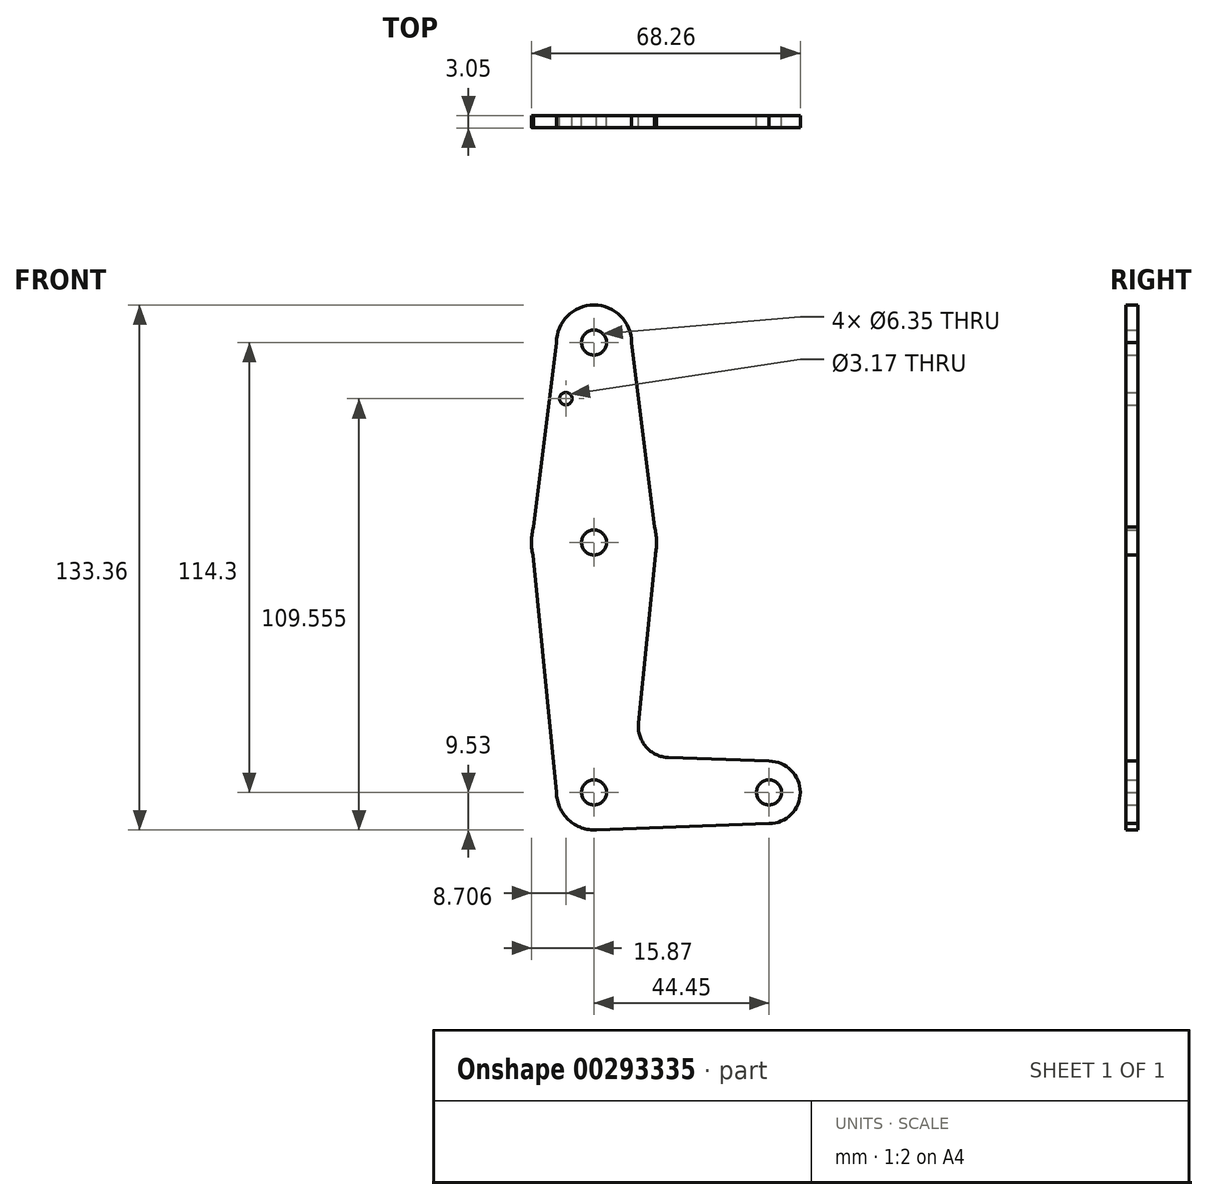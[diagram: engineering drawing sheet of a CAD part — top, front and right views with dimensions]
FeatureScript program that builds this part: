
annotation { "Feature Type Name" : "Feature", "Feature Type Description" : "" }
export const myFeature = defineFeature(function(context is Context, id is Id, definition is map)
    precondition{}
    {
        {
            var Q0;
            Q0=qCreatedBy(makeId("Front.planeOp"),FACE);
            var sketch = newSketch(context, id + "F0", { "sketchPlane" : qUnion([Q0])});
            skCircle(sketch, "E0", {"center": v(0, 0) * mm, "radius": 9.53 * mm});
            skLineSegment(sketch, "E1", {"start": v(0, 0) * mm, "end": v(0, 63.5) * mm, "construction": true});
            skCircle(sketch, "E2", {"center": v(0, 63.5) * mm, "radius": 15.88 * mm});
            skLineSegment(sketch, "E3", {"start": v(0, 63.5) * mm, "end": v(0, 114.3) * mm, "construction": true});
            skCircle(sketch, "E4", {"center": v(0, 114.3) * mm, "radius": 9.53 * mm});
            skLineSegment(sketch, "E5", {"start": v(0, 0) * mm, "end": v(44.45, 0) * mm, "construction": true});
            skCircle(sketch, "E6", {"center": v(44.45, 0) * mm, "radius": 7.94 * mm});
            skLineSegment(sketch, "E7", {"start": v(0, -9.53) * mm, "end": v(44.45, -7.94) * mm});
            skCircle(sketch, "E8", {"center": v(0, 114.3) * mm, "radius": 3.18 * mm});
            skCircle(sketch, "E9", {"center": v(0, 63.5) * mm, "radius": 3.17 * mm});
            skCircle(sketch, "E10", {"center": v(0, 0) * mm, "radius": 3.17 * mm});
            skCircle(sketch, "E11", {"center": v(44.45, 0) * mm, "radius": 3.17 * mm});
            skCircle(sketch, "E12", {"center": v(-7.16, 100.03) * mm, "radius": 1.59 * mm});
            skLineSegment(sketch, "E13", {"start": v(-9.52, 114.3) * mm, "end": v(-15.88, 63.5) * mm});
            skLineSegment(sketch, "E14", {"start": v(9.52, 114.3) * mm, "end": v(15.88, 63.5) * mm});
            skLineSegment(sketch, "E15", {"start": v(44.45, 7.94) * mm, "end": v(18.91, 8.85) * mm});
            skLineSegment(sketch, "E16", {"start": v(15.88, 63.5) * mm, "end": v(11.28, 17.59) * mm});
            skPoint(sketch, "E17.newPointA", {"position": v(9.52, 0) * mm});
            skPoint(sketch, "E17.newPointB", {"position": v(0, 9.53) * mm});
            skArc(sketch, "E17.filletArc", {"start": v(11.28, 17.59) * mm, "mid": v(13.2, 11.57) * mm, "end": v(18.91, 8.85) * mm});
            skLineSegment(sketch, "E18", {"start": v(-15.88, 63.5) * mm, "end": v(-9.52, 0) * mm});
            skSolve(sketch);
        }
        {
            var Q0;
            Q0 = qSketchRegion(id + "F0", true);
            extrude(context, id + "F1", {"entities" : qUnion([Q0]), "depth" : 3.05 * mm});
        }
    });
